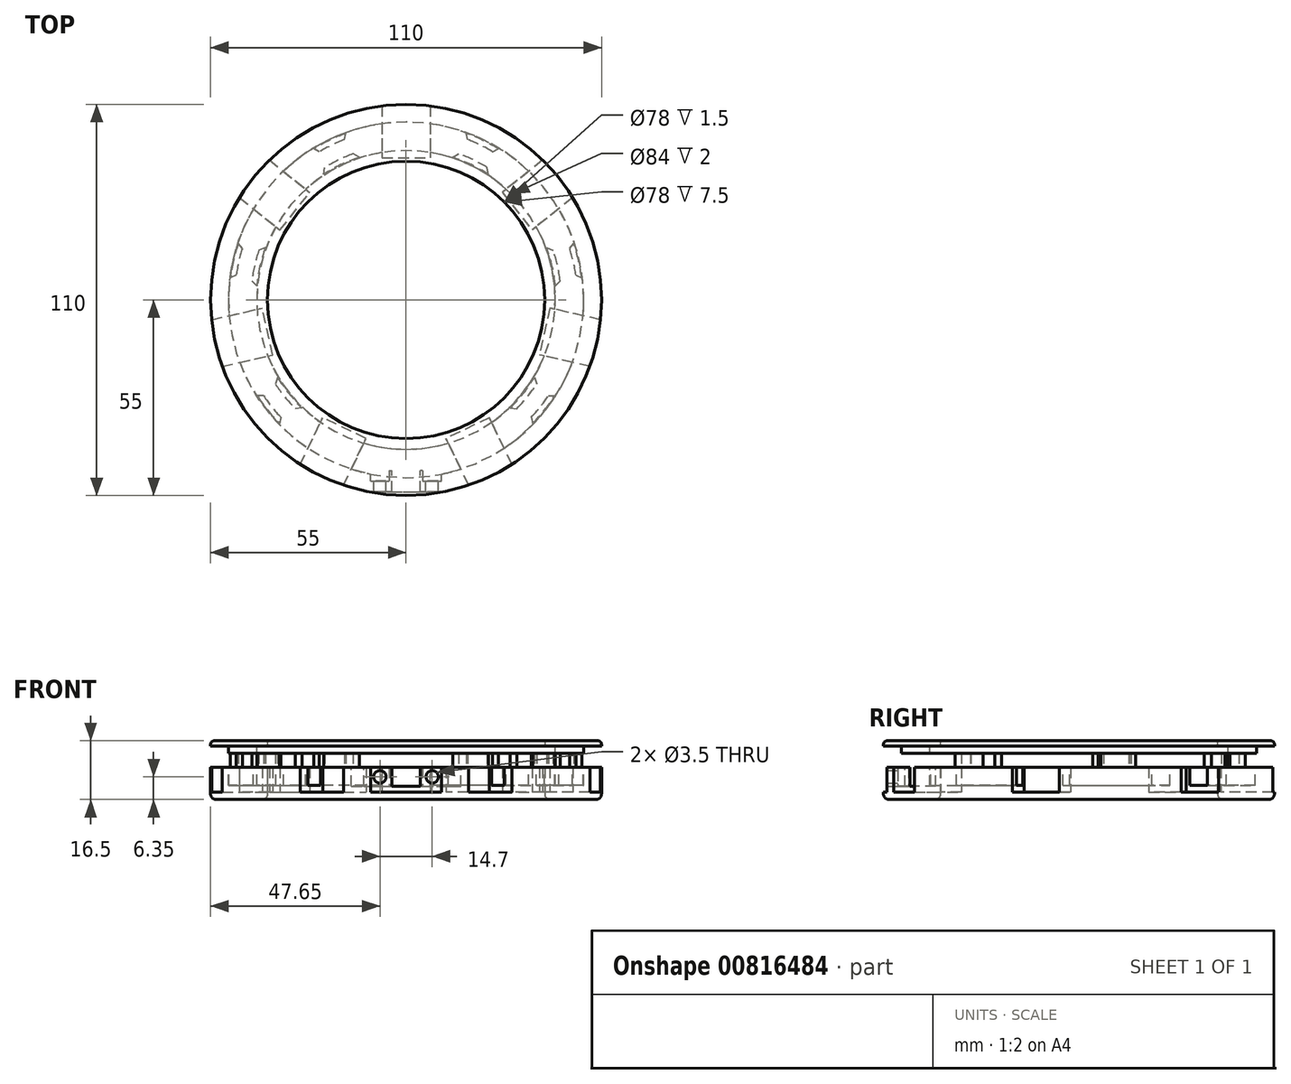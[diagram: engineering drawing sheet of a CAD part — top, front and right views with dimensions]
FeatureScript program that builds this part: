
annotation { "Feature Type Name" : "Feature", "Feature Type Description" : "" }
export const myFeature = defineFeature(function(context is Context, id is Id, definition is map)
    precondition{}
    {
        {
            var Q0;
            Q0=qCreatedBy(makeId("Top.planeOp"),FACE);
            var sketch = newSketch(context, id + "F0", { "sketchPlane" : qUnion([Q0])});
            skCircle(sketch, "E0", {"center": v(0, 0) * mm, "radius": 55 * mm});
            skCircle(sketch, "E1", {"center": v(0, 0) * mm, "radius": 39 * mm});
            skSolve(sketch);
        }
        {
            var Q0;
            Q0 = qSketchRegion(id + "F0", true);
            extrude(context, id + "F1", {"entities" : qUnion([Q0]), "depth" : 2 * mm, "offsetDistance" : 25 * mm});
        }
        {
            var Q0;
            Q0=makeQuery(id+"F1.opExtrude","CAP_FACE",FACE,{"disambiguationData":[OSD([sQuery(id+"F0.wireOp",EDGE,"E0"),sQuery(id+"F0.wireOp",EDGE,"E1")])],"isStart":false});
            var sketch = newSketch(context, id + "F2", { "sketchPlane" : qUnion([Q0])});
            skLineSegment(sketch, "E2.bottom", {"start": v(-6.75, 55) * mm, "end": v(6.75, 55) * mm});
            skLineSegment(sketch, "E2.top", {"start": v(-6.75, 40) * mm, "end": v(6.75, 40) * mm});
            skLineSegment(sketch, "E2.left", {"start": v(-6.75, 55) * mm, "end": v(-6.75, 40) * mm});
            skLineSegment(sketch, "E2.right", {"start": v(6.75, 55) * mm, "end": v(6.75, 40) * mm});
            skPoint(sketch, "E3", {"position": v(0, 55) * mm});
            skLineSegment(sketch, "E4.1.0", {"start": v(-47.2, 29.01) * mm, "end": v(-35.48, 19.66) * mm});
            skLineSegment(sketch, "E4.1.1", {"start": v(-47.2, 29.01) * mm, "end": v(-38.8, 39.57) * mm});
            skLineSegment(sketch, "E4.1.2", {"start": v(-38.8, 39.57) * mm, "end": v(-27.06, 30.22) * mm});
            skLineSegment(sketch, "E4.1.3", {"start": v(-35.48, 19.66) * mm, "end": v(-27.06, 30.22) * mm});
            skLineSegment(sketch, "E4.2.0", {"start": v(-52.12, -18.82) * mm, "end": v(-37.5, -15.48) * mm});
            skLineSegment(sketch, "E4.2.1", {"start": v(-52.12, -18.82) * mm, "end": v(-55.12, -5.66) * mm});
            skLineSegment(sketch, "E4.2.2", {"start": v(-55.12, -5.66) * mm, "end": v(-40.5, -2.32) * mm});
            skLineSegment(sketch, "E4.2.3", {"start": v(-37.5, -15.48) * mm, "end": v(-40.5, -2.32) * mm});
            skLineSegment(sketch, "E4.3.0", {"start": v(-17.78, -52.48) * mm, "end": v(-11.27, -38.97) * mm});
            skLineSegment(sketch, "E4.3.1", {"start": v(-17.78, -52.48) * mm, "end": v(-29.95, -46.62) * mm});
            skLineSegment(sketch, "E4.3.2", {"start": v(-29.95, -46.62) * mm, "end": v(-23.44, -33.11) * mm});
            skLineSegment(sketch, "E4.3.3", {"start": v(-11.27, -38.97) * mm, "end": v(-23.44, -33.11) * mm});
            skLineSegment(sketch, "E4.4.0", {"start": v(29.95, -46.62) * mm, "end": v(23.44, -33.11) * mm});
            skLineSegment(sketch, "E4.4.1", {"start": v(29.95, -46.62) * mm, "end": v(17.78, -52.48) * mm});
            skLineSegment(sketch, "E4.4.2", {"start": v(17.78, -52.48) * mm, "end": v(11.27, -38.97) * mm});
            skLineSegment(sketch, "E4.4.3", {"start": v(23.44, -33.11) * mm, "end": v(11.27, -38.97) * mm});
            skLineSegment(sketch, "E4.5.0", {"start": v(55.12, -5.66) * mm, "end": v(40.5, -2.32) * mm});
            skLineSegment(sketch, "E4.5.1", {"start": v(55.12, -5.66) * mm, "end": v(52.12, -18.82) * mm});
            skLineSegment(sketch, "E4.5.2", {"start": v(52.12, -18.82) * mm, "end": v(37.5, -15.48) * mm});
            skLineSegment(sketch, "E4.5.3", {"start": v(40.5, -2.32) * mm, "end": v(37.5, -15.48) * mm});
            skLineSegment(sketch, "E4.6.0", {"start": v(38.8, 39.57) * mm, "end": v(27.06, 30.22) * mm});
            skLineSegment(sketch, "E4.6.1", {"start": v(38.8, 39.57) * mm, "end": v(47.2, 29.01) * mm});
            skLineSegment(sketch, "E4.6.2", {"start": v(47.2, 29.01) * mm, "end": v(35.48, 19.66) * mm});
            skLineSegment(sketch, "E4.6.3", {"start": v(27.06, 30.22) * mm, "end": v(35.48, 19.66) * mm});
            skPoint(sketch, "E4.center", {"position": v(0, 0) * mm});
            skSolve(sketch);
        }
        {
            var Q0;
            {var subQ10=sQuery(id+"F2.wireOp",EDGE,"E2.top");Q0=makeQuery(id+"F2.imprint","IMPRINT",FACE,{"disambiguationData":[TD([[makeQuery(id+"F2.imprint","IMPRINT",EDGE,{"derivedFrom":subQ10}),-1.0]])]});}
            extrude(context, id + "F3", {"entities" : qUnion([Q0]), "operationType" : NewBodyOperationType.ADD, "depth" : 7 * mm, "offsetDistance" : 25 * mm});
        }
        {
            var Q0;
            Q0=makeQuery(id+"F3.opExtrude","CAP_FACE",FACE,{"disambiguationData":[OSD([sQuery(id+"F0.wireOp",EDGE,"E0"),sQuery(id+"F0.wireOp",EDGE,"E1"),sQuery(id+"F2.wireOp",EDGE,"E2.top"),sQuery(id+"F2.wireOp",EDGE,"E2.left"),sQuery(id+"F2.wireOp",EDGE,"E2.right"),sQuery(id+"F2.wireOp",EDGE,"E4.1.0"),sQuery(id+"F2.wireOp",EDGE,"E4.1.2"),sQuery(id+"F2.wireOp",EDGE,"E4.1.3"),sQuery(id+"F2.wireOp",EDGE,"E4.2.0"),sQuery(id+"F2.wireOp",EDGE,"E4.2.2"),sQuery(id+"F2.wireOp",EDGE,"E4.2.3"),sQuery(id+"F2.wireOp",EDGE,"E4.3.0"),sQuery(id+"F2.wireOp",EDGE,"E4.3.2"),sQuery(id+"F2.wireOp",EDGE,"E4.3.3"),sQuery(id+"F2.wireOp",EDGE,"E4.4.0"),sQuery(id+"F2.wireOp",EDGE,"E4.4.2"),sQuery(id+"F2.wireOp",EDGE,"E4.4.3"),sQuery(id+"F2.wireOp",EDGE,"E4.5.0"),sQuery(id+"F2.wireOp",EDGE,"E4.5.2"),sQuery(id+"F2.wireOp",EDGE,"E4.5.3"),sQuery(id+"F2.wireOp",EDGE,"E4.6.0"),sQuery(id+"F2.wireOp",EDGE,"E4.6.2"),sQuery(id+"F2.wireOp",EDGE,"E4.6.3")])],"isStart":false});
            var sketch = newSketch(context, id + "F4", { "sketchPlane" : qUnion([Q0])});
            skCircle(sketch, "E5", {"center": v(0, 0) * mm, "radius": 50 * mm});
            skCircle(sketch, "E6", {"center": v(0, 0) * mm, "radius": 42 * mm});
            skSolve(sketch);
        }
        {
            var Q0;
            Q0 = qSketchRegion(id + "F4", true);
            var Q1;
            {var subQ0=sQuery(id+"F0.wireOp",EDGE,"E0");Q1=makeQuery(id+"F3.boolean.opBoolean","SPLIT",FACE,{"disambiguationData":[TD([makeQuery(id+"F3.opExtrude","SWEPT_FACE",FACE,{"disambiguationData":[OSD([sQuery(id+"F2.wireOp",EDGE,"E2.top")])]})])],"derivedFrom":makeQuery(id+"F1.opExtrude","CAP_FACE",FACE,{"disambiguationData":[OSD([subQ0,sQuery(id+"F0.wireOp",EDGE,"E1")])],"isStart":false})});}
            extrude(context, id + "F5", {"entities" : qUnion([Q0]), "operationType" : NewBodyOperationType.REMOVE, "endBound" : BoundingType.UP_TO_SURFACE, "oppositeDirection" : true, "depth" : 25 * mm, "endBoundEntityFace" : qUnion([Q1]), "hasOffset" : true, "offsetDistance" : 2 * mm});
        }
        {
            var Q0;
            {var subQ0=sQuery(id+"F2.wireOp",EDGE,"E4.5.0");var subQ1=sQuery(id+"F0.wireOp",EDGE,"E0");var subQ2=makeQuery(id+"F1.opExtrude","CAP_EDGE",EDGE,{"disambiguationData":[OSD([subQ1])],"isStart":false});var subQ3=sQuery(id+"F2.wireOp",EDGE,"E4.6.2");var subQ4=sQuery(id+"F2.wireOp",EDGE,"E4.4.0");var subQ5=sQuery(id+"F2.wireOp",EDGE,"E4.5.2");var subQ6=sQuery(id+"F2.wireOp",EDGE,"E4.3.0");var subQ7=sQuery(id+"F2.wireOp",EDGE,"E4.4.2");var subQ8=sQuery(id+"F2.wireOp",EDGE,"E4.2.0");var subQ9=sQuery(id+"F2.wireOp",EDGE,"E4.3.2");var subQ10=sQuery(id+"F2.wireOp",EDGE,"E2.right");var subQ11=sQuery(id+"F2.wireOp",EDGE,"E4.6.0");var subQ12=sQuery(id+"F2.wireOp",EDGE,"E4.1.0");var subQ13=sQuery(id+"F2.wireOp",EDGE,"E4.2.2");var subQ14=sQuery(id+"F2.wireOp",EDGE,"E2.left");var subQ15=sQuery(id+"F2.wireOp",EDGE,"E4.1.2");Q0=makeQuery(id+"F5.boolean.opBoolean","SPLIT",FACE,{"disambiguationData":[TD([makeQuery(id+"F1.opExtrude","SWEPT_FACE",FACE,{"disambiguationData":[OSD([subQ1])]}),makeQuery(id+"F3.opExtrude","SWEPT_FACE",FACE,{"disambiguationData":[OSD([subQ6])]}),makeQuery(id+"F3.opExtrude","SWEPT_FACE",FACE,{"disambiguationData":[OSD([subQ7])]}),makeQuery(id+"F3.opExtrude","SWEPT_FACE",FACE,{"disambiguationData":[OSD([subQ1]),TDD([makeQuery(id+"F2.imprint","IMPRINT",EDGE,{"disambiguationData":[TD([[makeQuery(id+"F2.imprint","INTERSECT",VERTEX,{"derivedFrom":[subQ2,subQ14]}),-1.0]])],"derivedFrom":subQ2})])]}),makeQuery(id+"F3.opExtrude","SWEPT_FACE",FACE,{"disambiguationData":[OSD([subQ1]),TDD([makeQuery(id+"F2.imprint","IMPRINT",EDGE,{"disambiguationData":[TD([[makeQuery(id+"F2.imprint","INTERSECT",VERTEX,{"derivedFrom":[subQ2,subQ10]}),1.0]])],"derivedFrom":subQ2})])]}),makeQuery(id+"F3.opExtrude","SWEPT_FACE",FACE,{"disambiguationData":[OSD([subQ1]),TDD([makeQuery(id+"F2.imprint","IMPRINT",EDGE,{"disambiguationData":[TD([[makeQuery(id+"F2.imprint","INTERSECT",VERTEX,{"derivedFrom":[subQ2,subQ12]}),-1.0]])],"derivedFrom":subQ2})])]}),makeQuery(id+"F3.opExtrude","SWEPT_FACE",FACE,{"disambiguationData":[OSD([subQ1]),TDD([makeQuery(id+"F2.imprint","IMPRINT",EDGE,{"disambiguationData":[TD([[makeQuery(id+"F2.imprint","INTERSECT",VERTEX,{"derivedFrom":[subQ2,subQ8]}),-1.0]])],"derivedFrom":subQ2})])]}),makeQuery(id+"F3.opExtrude","SWEPT_FACE",FACE,{"disambiguationData":[OSD([subQ1]),TDD([makeQuery(id+"F2.imprint","IMPRINT",EDGE,{"disambiguationData":[TD([[makeQuery(id+"F2.imprint","INTERSECT",VERTEX,{"derivedFrom":[subQ2,subQ6]}),-1.0]])],"derivedFrom":subQ2})])]}),makeQuery(id+"F3.opExtrude","SWEPT_FACE",FACE,{"disambiguationData":[OSD([subQ1]),TDD([makeQuery(id+"F2.imprint","IMPRINT",EDGE,{"disambiguationData":[TD([[makeQuery(id+"F2.imprint","INTERSECT",VERTEX,{"derivedFrom":[subQ2,subQ4]}),-1.0]])],"derivedFrom":subQ2})])]}),makeQuery(id+"F3.opExtrude","SWEPT_FACE",FACE,{"disambiguationData":[OSD([subQ1]),TDD([makeQuery(id+"F2.imprint","IMPRINT",EDGE,{"disambiguationData":[TD([[makeQuery(id+"F2.imprint","INTERSECT",VERTEX,{"derivedFrom":[subQ2,subQ0]}),-1.0]])],"derivedFrom":subQ2})])]}),makeQuery(id+"F5.opExtrude","SWEPT_FACE",FACE,{"disambiguationData":[OSD([sQuery(id+"F4.wireOp",EDGE,"E5")])]})])],"derivedFrom":makeQuery(id+"F3.opExtrude","CAP_FACE",FACE,{"disambiguationData":[OSD([subQ1,sQuery(id+"F0.wireOp",EDGE,"E1"),sQuery(id+"F2.wireOp",EDGE,"E2.top"),subQ14,subQ10,subQ12,subQ15,sQuery(id+"F2.wireOp",EDGE,"E4.1.3"),subQ8,subQ13,sQuery(id+"F2.wireOp",EDGE,"E4.2.3"),subQ6,subQ9,sQuery(id+"F2.wireOp",EDGE,"E4.3.3"),subQ4,subQ7,sQuery(id+"F2.wireOp",EDGE,"E4.4.3"),subQ0,subQ5,sQuery(id+"F2.wireOp",EDGE,"E4.5.3"),subQ11,subQ3,sQuery(id+"F2.wireOp",EDGE,"E4.6.3")])],"isStart":false})});}
            var sketch = newSketch(context, id + "F6", { "sketchPlane" : qUnion([Q0])});
            skPoint(sketch, "E7.firstSnap0", {"position": v(0, -55) * mm});
            skLineSegment(sketch, "E7.bottom", {"start": v(10, -55) * mm, "end": v(-10, -55) * mm});
            skLineSegment(sketch, "E7.top", {"start": v(10, -54) * mm, "end": v(-10, -54) * mm});
            skLineSegment(sketch, "E7.left", {"start": v(10, -55) * mm, "end": v(10, -54) * mm});
            skLineSegment(sketch, "E7.right", {"start": v(-10, -55) * mm, "end": v(-10, -54) * mm});
            skLineSegment(sketch, "E8.bottom", {"start": v(-10, -51) * mm, "end": v(10, -51) * mm});
            skLineSegment(sketch, "E8.top", {"start": v(-10, -48.99) * mm, "end": v(10, -48.99) * mm});
            skLineSegment(sketch, "E8.left", {"start": v(-10, -51) * mm, "end": v(-10, -48.99) * mm});
            skLineSegment(sketch, "E8.right", {"start": v(10, -51) * mm, "end": v(10, -48.99) * mm});
            skSolve(sketch);
        }
        {
            var Q0;
            {var subQ7=sQuery(id+"F6.wireOp",EDGE,"E7.top");Q0=makeQuery(id+"F6.imprint","IMPRINT",FACE,{"disambiguationData":[TD([[makeQuery(id+"F6.imprint","IMPRINT",EDGE,{"derivedFrom":subQ7}),1.0]])]});}
            var Q1;
            {var subQ0=sQuery(id+"F0.wireOp",EDGE,"E0");var subQ2=sQuery(id+"F2.wireOp",EDGE,"E4.3.0");Q1=makeQuery(id+"F3.boolean.opBoolean","SPLIT",FACE,{"disambiguationData":[TD([makeQuery(id+"F3.opExtrude","SWEPT_FACE",FACE,{"disambiguationData":[OSD([subQ2])]})])],"derivedFrom":makeQuery(id+"F1.opExtrude","CAP_FACE",FACE,{"disambiguationData":[OSD([subQ0,sQuery(id+"F0.wireOp",EDGE,"E1")])],"isStart":false})});}
            extrude(context, id + "F7", {"entities" : qUnion([Q0]), "operationType" : NewBodyOperationType.REMOVE, "endBound" : BoundingType.UP_TO_SURFACE, "oppositeDirection" : true, "depth" : 25 * mm, "endBoundEntityFace" : qUnion([Q1]), "offsetDistance" : 25 * mm});
        }
        {
            var Q0;
            Q0=makeQuery(id+"F6.imprint","IMPRINT",FACE,{"disambiguationData":[TD([[makeQuery(id+"F6.imprint","IMPRINT",EDGE,{"derivedFrom":sQuery(id+"F6.wireOp",EDGE,"E8.bottom")}),1.0]])]});
            extrude(context, id + "F8", {"entities" : qUnion([Q0]), "operationType" : NewBodyOperationType.REMOVE, "oppositeDirection" : true, "depth" : 5.3 * mm, "offsetDistance" : 25 * mm});
        }
        {
            var Q0;
            {var subQ0=sQuery(id+"F2.wireOp",EDGE,"E4.5.0");var subQ1=sQuery(id+"F0.wireOp",EDGE,"E0");var subQ2=makeQuery(id+"F1.opExtrude","CAP_EDGE",EDGE,{"disambiguationData":[OSD([subQ1])],"isStart":false});var subQ3=sQuery(id+"F2.wireOp",EDGE,"E4.6.2");var subQ4=sQuery(id+"F2.wireOp",EDGE,"E4.4.0");var subQ5=sQuery(id+"F2.wireOp",EDGE,"E4.5.2");var subQ6=sQuery(id+"F2.wireOp",EDGE,"E4.3.0");var subQ7=sQuery(id+"F2.wireOp",EDGE,"E4.4.2");var subQ8=sQuery(id+"F2.wireOp",EDGE,"E4.2.0");var subQ9=sQuery(id+"F2.wireOp",EDGE,"E4.3.2");var subQ10=sQuery(id+"F2.wireOp",EDGE,"E2.right");var subQ11=sQuery(id+"F2.wireOp",EDGE,"E4.6.0");var subQ12=sQuery(id+"F2.wireOp",EDGE,"E4.1.0");var subQ13=sQuery(id+"F2.wireOp",EDGE,"E4.2.2");var subQ14=sQuery(id+"F2.wireOp",EDGE,"E2.left");var subQ15=sQuery(id+"F2.wireOp",EDGE,"E4.1.2");Q0=makeQuery(id+"F5.boolean.opBoolean","SPLIT",FACE,{"disambiguationData":[TD([makeQuery(id+"F1.opExtrude","SWEPT_FACE",FACE,{"disambiguationData":[OSD([subQ1])]}),makeQuery(id+"F3.opExtrude","SWEPT_FACE",FACE,{"disambiguationData":[OSD([subQ6])]}),makeQuery(id+"F3.opExtrude","SWEPT_FACE",FACE,{"disambiguationData":[OSD([subQ7])]}),makeQuery(id+"F3.opExtrude","SWEPT_FACE",FACE,{"disambiguationData":[OSD([subQ1]),TDD([makeQuery(id+"F2.imprint","IMPRINT",EDGE,{"disambiguationData":[TD([[makeQuery(id+"F2.imprint","INTERSECT",VERTEX,{"derivedFrom":[subQ2,subQ14]}),-1.0]])],"derivedFrom":subQ2})])]}),makeQuery(id+"F3.opExtrude","SWEPT_FACE",FACE,{"disambiguationData":[OSD([subQ1]),TDD([makeQuery(id+"F2.imprint","IMPRINT",EDGE,{"disambiguationData":[TD([[makeQuery(id+"F2.imprint","INTERSECT",VERTEX,{"derivedFrom":[subQ2,subQ10]}),1.0]])],"derivedFrom":subQ2})])]}),makeQuery(id+"F3.opExtrude","SWEPT_FACE",FACE,{"disambiguationData":[OSD([subQ1]),TDD([makeQuery(id+"F2.imprint","IMPRINT",EDGE,{"disambiguationData":[TD([[makeQuery(id+"F2.imprint","INTERSECT",VERTEX,{"derivedFrom":[subQ2,subQ12]}),-1.0]])],"derivedFrom":subQ2})])]}),makeQuery(id+"F3.opExtrude","SWEPT_FACE",FACE,{"disambiguationData":[OSD([subQ1]),TDD([makeQuery(id+"F2.imprint","IMPRINT",EDGE,{"disambiguationData":[TD([[makeQuery(id+"F2.imprint","INTERSECT",VERTEX,{"derivedFrom":[subQ2,subQ8]}),-1.0]])],"derivedFrom":subQ2})])]}),makeQuery(id+"F3.opExtrude","SWEPT_FACE",FACE,{"disambiguationData":[OSD([subQ1]),TDD([makeQuery(id+"F2.imprint","IMPRINT",EDGE,{"disambiguationData":[TD([[makeQuery(id+"F2.imprint","INTERSECT",VERTEX,{"derivedFrom":[subQ2,subQ6]}),-1.0]])],"derivedFrom":subQ2})])]}),makeQuery(id+"F3.opExtrude","SWEPT_FACE",FACE,{"disambiguationData":[OSD([subQ1]),TDD([makeQuery(id+"F2.imprint","IMPRINT",EDGE,{"disambiguationData":[TD([[makeQuery(id+"F2.imprint","INTERSECT",VERTEX,{"derivedFrom":[subQ2,subQ4]}),-1.0]])],"derivedFrom":subQ2})])]}),makeQuery(id+"F3.opExtrude","SWEPT_FACE",FACE,{"disambiguationData":[OSD([subQ1]),TDD([makeQuery(id+"F2.imprint","IMPRINT",EDGE,{"disambiguationData":[TD([[makeQuery(id+"F2.imprint","INTERSECT",VERTEX,{"derivedFrom":[subQ2,subQ0]}),-1.0]])],"derivedFrom":subQ2})])]}),makeQuery(id+"F5.opExtrude","SWEPT_FACE",FACE,{"disambiguationData":[OSD([sQuery(id+"F4.wireOp",EDGE,"E5")])]})])],"derivedFrom":makeQuery(id+"F3.opExtrude","CAP_FACE",FACE,{"disambiguationData":[OSD([subQ1,sQuery(id+"F0.wireOp",EDGE,"E1"),sQuery(id+"F2.wireOp",EDGE,"E2.top"),subQ14,subQ10,subQ12,subQ15,sQuery(id+"F2.wireOp",EDGE,"E4.1.3"),subQ8,subQ13,sQuery(id+"F2.wireOp",EDGE,"E4.2.3"),subQ6,subQ9,sQuery(id+"F2.wireOp",EDGE,"E4.3.3"),subQ4,subQ7,sQuery(id+"F2.wireOp",EDGE,"E4.4.3"),subQ0,subQ5,sQuery(id+"F2.wireOp",EDGE,"E4.5.3"),subQ11,subQ3,sQuery(id+"F2.wireOp",EDGE,"E4.6.3")])],"isStart":false})});}
            var sketch = newSketch(context, id + "F9", { "sketchPlane" : qUnion([Q0])});
            skLineSegment(sketch, "E9", {"start": v(-4, -51) * mm, "end": v(-4, -54) * mm});
            skLineSegment(sketch, "E10.MirrorCS", {"start": v(4, -51) * mm, "end": v(4, -54) * mm});
            skSolve(sketch);
        }
        {
            var Q0;
            {var subQ0=sQuery(id+"F9.wireOp",EDGE,"E9");Q0=makeQuery(id+"F9.imprint","IMPRINT",FACE,{"disambiguationData":[TD([[makeQuery(id+"F9.imprint","IMPRINT",EDGE,{"derivedFrom":subQ0}),1.0]])]});}
            var Q1;
            Q1=makeQuery(id+"F8.boolean.opBoolean","COPY",FACE,{"derivedFrom":makeQuery(id+"F8.opExtrude","CAP_FACE",FACE,{"disambiguationData":[OSD([sQuery(id+"F4.wireOp",EDGE,"E5"),sQuery(id+"F6.wireOp",EDGE,"E8.bottom"),sQuery(id+"F6.wireOp",EDGE,"E8.left"),sQuery(id+"F6.wireOp",EDGE,"E8.right")])],"isStart":false})});
            extrude(context, id + "F10", {"entities" : qUnion([Q0]), "operationType" : NewBodyOperationType.REMOVE, "endBound" : BoundingType.UP_TO_SURFACE, "oppositeDirection" : true, "depth" : 25 * mm, "endBoundEntityFace" : qUnion([Q1]), "offsetDistance" : 25 * mm});
        }
        {
            var Q0;
            {var subQ0=sQuery(id+"F4.wireOp",EDGE,"E5");var subQ1=sQuery(id+"F4.wireOp",EDGE,"E6");Q0=makeQuery(id+"F5.boolean.opBoolean","COPY",FACE,{"disambiguationData":[TD([makeQuery(id+"F3.opExtrude","SWEPT_FACE",FACE,{"disambiguationData":[OSD([sQuery(id+"F2.wireOp",EDGE,"E4.3.0")])]})])],"derivedFrom":makeQuery(id+"F5.opExtrude","CAP_FACE",FACE,{"disambiguationData":[OSD([subQ0,subQ1])],"isStart":false})});}
            var Q1;
            {var subQ0=sQuery(id+"F6.wireOp",EDGE,"E8.bottom");Q1=makeQuery(id+"F10.boolean.opBoolean","MERGE",FACE,{"derivedFrom":[makeQuery(id+"F8.boolean.opBoolean","COPY",FACE,{"derivedFrom":makeQuery(id+"F8.opExtrude","CAP_FACE",FACE,{"disambiguationData":[OSD([sQuery(id+"F4.wireOp",EDGE,"E5"),subQ0,sQuery(id+"F6.wireOp",EDGE,"E8.left"),sQuery(id+"F6.wireOp",EDGE,"E8.right")])],"isStart":false})})],"fromTools":[makeQuery(id+"F10.opExtrude","CAP_FACE",FACE,{"disambiguationData":[OSD([sQuery(id+"F6.wireOp",EDGE,"E7.top"),subQ0,sQuery(id+"F9.wireOp",EDGE,"E9"),sQuery(id+"F9.wireOp",EDGE,"E10.MirrorCS")])],"isStart":false})]});}
            extrude(context, id + "F11", {"entities" : qUnion([Q0]), "operationType" : NewBodyOperationType.REMOVE, "endBound" : BoundingType.UP_TO_SURFACE, "oppositeDirection" : true, "depth" : 25 * mm, "endBoundEntityFace" : qUnion([Q1]), "offsetDistance" : 25 * mm});
        }
        {
            var Q0;
            {var subQ0=sQuery(id+"F4.wireOp",EDGE,"E5");var subQ1=sQuery(id+"F6.wireOp",EDGE,"E8.bottom");Q0=makeQuery(id+"F11.boolean.opBoolean","MERGE",FACE,{"derivedFrom":[makeQuery(id+"F10.boolean.opBoolean","MERGE",FACE,{"derivedFrom":[makeQuery(id+"F8.boolean.opBoolean","COPY",FACE,{"derivedFrom":makeQuery(id+"F8.opExtrude","CAP_FACE",FACE,{"disambiguationData":[OSD([subQ0,subQ1,sQuery(id+"F6.wireOp",EDGE,"E8.left"),sQuery(id+"F6.wireOp",EDGE,"E8.right")])],"isStart":false})})],"fromTools":[makeQuery(id+"F10.opExtrude","CAP_FACE",FACE,{"disambiguationData":[OSD([sQuery(id+"F6.wireOp",EDGE,"E7.top"),subQ1,sQuery(id+"F9.wireOp",EDGE,"E9"),sQuery(id+"F9.wireOp",EDGE,"E10.MirrorCS")])],"isStart":false})]})],"fromTools":[makeQuery(id+"F11.opExtrude","CAP_FACE",FACE,{"disambiguationData":[OSD([subQ0,sQuery(id+"F4.wireOp",EDGE,"E6")])],"isStart":false})]});}
            var sketch = newSketch(context, id + "F12", { "sketchPlane" : qUnion([Q0])});
            skLineSegment(sketch, "E11.top", {"start": v(-4.7, -51) * mm, "end": v(-4, -51) * mm});
            skLineSegment(sketch, "E11.left", {"start": v(-4.7, -48) * mm, "end": v(-4.7, -51) * mm});
            skLineSegment(sketch, "E11.right", {"start": v(-4, -48) * mm, "end": v(-4, -51) * mm});
            skLineSegment(sketch, "E12", {"start": v(-4.7, -48) * mm, "end": v(-4, -48) * mm});
            skLineSegment(sketch, "E13.MirrorCS", {"start": v(4.7, -51) * mm, "end": v(4, -51) * mm});
            skLineSegment(sketch, "E14.MirrorCS", {"start": v(4.7, -48) * mm, "end": v(4, -48) * mm});
            skLineSegment(sketch, "E15.MirrorCS", {"start": v(4, -48) * mm, "end": v(4, -51) * mm});
            skLineSegment(sketch, "E16.MirrorCS", {"start": v(4.7, -48) * mm, "end": v(4.7, -51) * mm});
            skSolve(sketch);
        }
        {
            var Q0;
            Q0 = qSketchRegion(id + "F12", true);
            var Q1;
            {var subQ0=sQuery(id+"F2.wireOp",EDGE,"E4.5.0");var subQ1=sQuery(id+"F0.wireOp",EDGE,"E0");var subQ2=makeQuery(id+"F1.opExtrude","CAP_EDGE",EDGE,{"disambiguationData":[OSD([subQ1])],"isStart":false});var subQ3=sQuery(id+"F2.wireOp",EDGE,"E4.6.2");var subQ4=makeQuery(id+"F3.opExtrude","SWEPT_FACE",FACE,{"disambiguationData":[OSD([subQ1]),TDD([makeQuery(id+"F2.imprint","IMPRINT",EDGE,{"disambiguationData":[TD([[makeQuery(id+"F2.imprint","INTERSECT",VERTEX,{"derivedFrom":[subQ2,subQ0]}),-1.0]])],"derivedFrom":subQ2})])]});var subQ5=sQuery(id+"F2.wireOp",EDGE,"E4.4.0");var subQ6=sQuery(id+"F2.wireOp",EDGE,"E4.5.2");var subQ7=makeQuery(id+"F3.opExtrude","SWEPT_FACE",FACE,{"disambiguationData":[OSD([subQ1]),TDD([makeQuery(id+"F2.imprint","IMPRINT",EDGE,{"disambiguationData":[TD([[makeQuery(id+"F2.imprint","INTERSECT",VERTEX,{"derivedFrom":[subQ2,subQ5]}),-1.0]])],"derivedFrom":subQ2})])]});var subQ8=sQuery(id+"F2.wireOp",EDGE,"E4.3.0");var subQ9=sQuery(id+"F2.wireOp",EDGE,"E4.4.2");var subQ10=makeQuery(id+"F3.opExtrude","SWEPT_FACE",FACE,{"disambiguationData":[OSD([subQ1]),TDD([makeQuery(id+"F2.imprint","IMPRINT",EDGE,{"disambiguationData":[TD([[makeQuery(id+"F2.imprint","INTERSECT",VERTEX,{"derivedFrom":[subQ2,subQ8]}),-1.0]])],"derivedFrom":subQ2})])]});var subQ11=sQuery(id+"F2.wireOp",EDGE,"E4.2.0");var subQ12=sQuery(id+"F2.wireOp",EDGE,"E4.3.2");var subQ13=makeQuery(id+"F3.opExtrude","SWEPT_FACE",FACE,{"disambiguationData":[OSD([subQ1]),TDD([makeQuery(id+"F2.imprint","IMPRINT",EDGE,{"disambiguationData":[TD([[makeQuery(id+"F2.imprint","INTERSECT",VERTEX,{"derivedFrom":[subQ2,subQ11]}),-1.0]])],"derivedFrom":subQ2})])]});var subQ14=sQuery(id+"F2.wireOp",EDGE,"E4.1.0");var subQ15=sQuery(id+"F2.wireOp",EDGE,"E4.2.2");var subQ16=makeQuery(id+"F3.opExtrude","SWEPT_FACE",FACE,{"disambiguationData":[OSD([subQ1]),TDD([makeQuery(id+"F2.imprint","IMPRINT",EDGE,{"disambiguationData":[TD([[makeQuery(id+"F2.imprint","INTERSECT",VERTEX,{"derivedFrom":[subQ2,subQ14]}),-1.0]])],"derivedFrom":subQ2})])]});var subQ17=makeQuery(id+"F1.opExtrude","SWEPT_FACE",FACE,{"disambiguationData":[OSD([subQ1])]});var subQ18=makeQuery(id+"F3.opExtrude","SWEPT_FACE",FACE,{"disambiguationData":[OSD([subQ8])]});var subQ19=sQuery(id+"F2.wireOp",EDGE,"E4.6.0");var subQ20=sQuery(id+"F2.wireOp",EDGE,"E4.1.2");var subQ21=sQuery(id+"F2.wireOp",EDGE,"E2.right");var subQ22=sQuery(id+"F2.wireOp",EDGE,"E2.left");var subQ23=makeQuery(id+"F3.opExtrude","CAP_FACE",FACE,{"disambiguationData":[OSD([subQ1,sQuery(id+"F0.wireOp",EDGE,"E1"),sQuery(id+"F2.wireOp",EDGE,"E2.top"),subQ22,subQ21,subQ14,subQ20,sQuery(id+"F2.wireOp",EDGE,"E4.1.3"),subQ11,subQ15,sQuery(id+"F2.wireOp",EDGE,"E4.2.3"),subQ8,subQ12,sQuery(id+"F2.wireOp",EDGE,"E4.3.3"),subQ5,subQ9,sQuery(id+"F2.wireOp",EDGE,"E4.4.3"),subQ0,subQ6,sQuery(id+"F2.wireOp",EDGE,"E4.5.3"),subQ19,subQ3,sQuery(id+"F2.wireOp",EDGE,"E4.6.3")])],"isStart":false});var subQ24=sQuery(id+"F4.wireOp",EDGE,"E5");var subQ25=makeQuery(id+"F3.opExtrude","SWEPT_FACE",FACE,{"disambiguationData":[OSD([subQ9])]});var subQ26=makeQuery(id+"F5.opExtrude","SWEPT_FACE",FACE,{"disambiguationData":[OSD([subQ24])]});var subQ27=makeQuery(id+"F3.opExtrude","SWEPT_FACE",FACE,{"disambiguationData":[OSD([subQ1]),TDD([makeQuery(id+"F2.imprint","IMPRINT",EDGE,{"disambiguationData":[TD([[makeQuery(id+"F2.imprint","INTERSECT",VERTEX,{"derivedFrom":[subQ2,subQ21]}),1.0]])],"derivedFrom":subQ2})])]});var subQ28=makeQuery(id+"F3.opExtrude","SWEPT_FACE",FACE,{"disambiguationData":[OSD([subQ1]),TDD([makeQuery(id+"F2.imprint","IMPRINT",EDGE,{"disambiguationData":[TD([[makeQuery(id+"F2.imprint","INTERSECT",VERTEX,{"derivedFrom":[subQ2,subQ22]}),-1.0]])],"derivedFrom":subQ2})])]});Q1=makeQuery(id+"F10.boolean.opBoolean","SPLIT",FACE,{"disambiguationData":[TD([subQ18])],"derivedFrom":makeQuery(id+"F5.boolean.opBoolean","SPLIT",FACE,{"disambiguationData":[TD([subQ17,subQ18,subQ25,subQ28,subQ27,subQ16,subQ13,subQ10,subQ7,subQ4,subQ26])],"derivedFrom":subQ23})});}
            extrude(context, id + "F13", {"entities" : qUnion([Q0]), "operationType" : NewBodyOperationType.ADD, "endBound" : BoundingType.UP_TO_SURFACE, "depth" : 25 * mm, "endBoundEntityFace" : qUnion([Q1]), "offsetDistance" : 25 * mm});
        }
        {
            var Q0;
            {var subQ1=sQuery(id+"F6.wireOp",EDGE,"E8.left");var subQ2=sQuery(id+"F6.wireOp",EDGE,"E8.bottom");Q0=makeQuery(id+"F10.boolean.opBoolean","SPLIT",FACE,{"disambiguationData":[TD([makeQuery(id+"F8.boolean.opBoolean","COPY",FACE,{"derivedFrom":makeQuery(id+"F8.opExtrude","SWEPT_FACE",FACE,{"disambiguationData":[OSD([subQ1])]})})])],"derivedFrom":makeQuery(id+"F8.boolean.opBoolean","COPY",FACE,{"derivedFrom":makeQuery(id+"F8.opExtrude","SWEPT_FACE",FACE,{"disambiguationData":[OSD([subQ2])]})})});}
            var sketch = newSketch(context, id + "F14", { "sketchPlane" : qUnion([Q0])});
            skCircle(sketch, "E17", {"center": v(7.35, 6.35) * mm, "radius": 1.75 * mm});
            skPoint(sketch, "E17.centerSnap0", {"position": v(10, 6.35) * mm});
            skPoint(sketch, "E17.centerSnap1", {"position": v(7.35, 9) * mm});
            skCircle(sketch, "E18.MirrorC", {"center": v(-7.35, 6.35) * mm, "radius": 1.75 * mm});
            skSolve(sketch);
        }
        {
            var Q0;
            Q0 = qSketchRegion(id + "F14", true);
            var Q1;
            Q1=makeQuery(id+"F7.boolean.opBoolean","COPY",FACE,{"derivedFrom":makeQuery(id+"F7.opExtrude","SWEPT_FACE",FACE,{"disambiguationData":[OSD([sQuery(id+"F6.wireOp",EDGE,"E7.top")])]})});
            extrude(context, id + "F15", {"entities" : qUnion([Q0]), "operationType" : NewBodyOperationType.REMOVE, "endBound" : BoundingType.UP_TO_SURFACE, "oppositeDirection" : true, "depth" : 25 * mm, "endBoundEntityFace" : qUnion([Q1]), "offsetDistance" : 25 * mm});
        }
        {
            var Q0;
            Q0=makeQuery(id+"F1.opExtrude","CAP_EDGE",EDGE,{"disambiguationData":[OSD([sQuery(id+"F0.wireOp",EDGE,"E0")])],"isStart":true});
            var Q1;
            Q1=makeQuery(id+"F1.opExtrude","CAP_EDGE",EDGE,{"disambiguationData":[OSD([sQuery(id+"F0.wireOp",EDGE,"E1")])],"isStart":true});
            fillet(context, id + "F16", {"entities" : qUnion([Q0, Q1]), "radius" : 1.5 * mm, "tangentPropagation" : true, "allowEdgeOverflow" : false});
        }
        {
            var Q0;
            {var subQ1=sQuery(id+"F2.wireOp",EDGE,"E2.left");var subQ7=sQuery(id+"F0.wireOp",EDGE,"E0");var subQ8=makeQuery(id+"F1.opExtrude","CAP_EDGE",EDGE,{"disambiguationData":[OSD([subQ7])],"isStart":false});var subQ9=makeQuery(id+"F3.opExtrude","CAP_EDGE",EDGE,{"disambiguationData":[OSD([subQ7]),TDD([makeQuery(id+"F2.imprint","IMPRINT",EDGE,{"disambiguationData":[TD([[makeQuery(id+"F2.imprint","INTERSECT",VERTEX,{"derivedFrom":[subQ8,subQ1]}),-1.0]])],"derivedFrom":subQ8})])],"isStart":false});Q0=makeQuery(id+"F4.imprint","IMPRINT",FACE,{"disambiguationData":[TD([[makeQuery(id+"F4.imprint","IMPRINT",EDGE,{"derivedFrom":subQ9}),1.0]])]});}
            var sketch = newSketch(context, id + "F17", { "sketchPlane" : qUnion([Q0])});
            skPoint(sketch, "E19.0", {"position": v(0, 55) * mm});
            skArc(sketch, "E20", {"start": v(-17, 46.81) * mm, "mid": v(-21.6, 44.87) * mm, "end": v(-26, 42.47) * mm});
            skArc(sketch, "E21", {"start": v(-13.15, 40.1) * mm, "mid": v(-18.3, 38.02) * mm, "end": v(-23.15, 35.28) * mm});
            skArc(sketch, "E22", {"start": v(-17.39, 45.06) * mm, "mid": v(-20.96, 43.52) * mm, "end": v(-24.39, 41.7) * mm});
            skArc(sketch, "E23", {"start": v(-22.86, 37.24) * mm, "mid": v(-18.96, 39.37) * mm, "end": v(-14.86, 41.1) * mm});
            skLineSegment(sketch, "E24", {"start": v(-26, 42.47) * mm, "end": v(-24.39, 41.7) * mm});
            skLineSegment(sketch, "E25", {"start": v(-17, 46.81) * mm, "end": v(-17.39, 45.06) * mm});
            skLineSegment(sketch, "E26", {"start": v(-22.86, 37.24) * mm, "end": v(-23.15, 35.28) * mm});
            skLineSegment(sketch, "E27", {"start": v(-14.86, 41.1) * mm, "end": v(-13.15, 40.1) * mm});
            skPoint(sketch, "E28", {"position": v(-18.3, 38.02) * mm});
            skPoint(sketch, "E29", {"position": v(-18.96, 39.37) * mm});
            skPoint(sketch, "E30", {"position": v(-20.96, 43.52) * mm});
            skPoint(sketch, "E31", {"position": v(-21.6, 44.87) * mm});
            skLineSegment(sketch, "E32", {"start": v(-21.6, 44.87) * mm, "end": v(0, 0) * mm, "construction": true});
            skArc(sketch, "E33.1.0", {"start": v(-46.07, 14.5) * mm, "mid": v(-47.09, 10.75) * mm, "end": v(-47.8, 6.93) * mm});
            skArc(sketch, "E33.1.1", {"start": v(-43.37, 5.35) * mm, "mid": v(-42.6, 9.72) * mm, "end": v(-41.4, 14) * mm});
            skArc(sketch, "E33.1.2", {"start": v(-39.55, 14.72) * mm, "mid": v(-41.14, 9.4) * mm, "end": v(-42.02, 3.9) * mm});
            skLineSegment(sketch, "E33.1.3", {"start": v(-49.42, 6.15) * mm, "end": v(-47.8, 6.93) * mm});
            skArc(sketch, "E33.1.4", {"start": v(-47.2, 15.9) * mm, "mid": v(-48.55, 11.08) * mm, "end": v(-49.42, 6.15) * mm});
            skLineSegment(sketch, "E33.1.5", {"start": v(-47.2, 15.9) * mm, "end": v(-46.07, 14.5) * mm});
            skLineSegment(sketch, "E33.1.6", {"start": v(-43.37, 5.35) * mm, "end": v(-42.02, 3.9) * mm});
            skLineSegment(sketch, "E33.1.7", {"start": v(-41.4, 14) * mm, "end": v(-39.55, 14.72) * mm});
            skPoint(sketch, "E33.1.8", {"position": v(-42.6, 9.72) * mm});
            skPoint(sketch, "E33.1.9", {"position": v(-47.09, 10.75) * mm});
            skPoint(sketch, "E33.1.10", {"position": v(-48.55, 11.08) * mm});
            skPoint(sketch, "E33.1.11", {"position": v(-41.14, 9.4) * mm});
            skArc(sketch, "E33.2.0", {"start": v(-40.06, -26.98) * mm, "mid": v(-37.76, -30.11) * mm, "end": v(-35.22, -33.05) * mm});
            skArc(sketch, "E33.2.1", {"start": v(-31.22, -30.58) * mm, "mid": v(-34.17, -27.25) * mm, "end": v(-36.76, -23.63) * mm});
            skArc(sketch, "E33.2.2", {"start": v(-36.17, -21.74) * mm, "mid": v(-33, -26.31) * mm, "end": v(-29.25, -30.42) * mm});
            skLineSegment(sketch, "E33.2.3", {"start": v(-35.62, -34.8) * mm, "end": v(-35.22, -33.05) * mm});
            skArc(sketch, "E33.2.4", {"start": v(-41.86, -26.98) * mm, "mid": v(-38.94, -31.05) * mm, "end": v(-35.62, -34.8) * mm});
            skLineSegment(sketch, "E33.2.5", {"start": v(-41.86, -26.98) * mm, "end": v(-40.06, -26.98) * mm});
            skLineSegment(sketch, "E33.2.6", {"start": v(-31.22, -30.58) * mm, "end": v(-29.25, -30.42) * mm});
            skLineSegment(sketch, "E33.2.7", {"start": v(-36.76, -23.63) * mm, "end": v(-36.17, -21.74) * mm});
            skPoint(sketch, "E33.2.8", {"position": v(-34.17, -27.25) * mm});
            skPoint(sketch, "E33.2.9", {"position": v(-37.76, -30.11) * mm});
            skPoint(sketch, "E33.2.10", {"position": v(-38.94, -31.05) * mm});
            skPoint(sketch, "E33.2.11", {"position": v(-33, -26.31) * mm});
            skArc(sketch, "E33.4.0", {"start": v(35.22, -33.05) * mm, "mid": v(37.76, -30.11) * mm, "end": v(40.06, -26.98) * mm});
            skArc(sketch, "E33.4.1", {"start": v(36.76, -23.63) * mm, "mid": v(34.17, -27.25) * mm, "end": v(31.22, -30.58) * mm});
            skArc(sketch, "E33.4.2", {"start": v(29.25, -30.42) * mm, "mid": v(33, -26.31) * mm, "end": v(36.17, -21.74) * mm});
            skLineSegment(sketch, "E33.4.3", {"start": v(41.86, -26.98) * mm, "end": v(40.06, -26.98) * mm});
            skArc(sketch, "E33.4.4", {"start": v(35.62, -34.8) * mm, "mid": v(38.94, -31.05) * mm, "end": v(41.86, -26.98) * mm});
            skLineSegment(sketch, "E33.4.5", {"start": v(35.62, -34.8) * mm, "end": v(35.22, -33.05) * mm});
            skLineSegment(sketch, "E33.4.6", {"start": v(36.76, -23.63) * mm, "end": v(36.17, -21.74) * mm});
            skLineSegment(sketch, "E33.4.7", {"start": v(31.22, -30.58) * mm, "end": v(29.25, -30.42) * mm});
            skPoint(sketch, "E33.4.8", {"position": v(34.17, -27.25) * mm});
            skPoint(sketch, "E33.4.9", {"position": v(37.76, -30.11) * mm});
            skPoint(sketch, "E33.4.10", {"position": v(38.94, -31.05) * mm});
            skPoint(sketch, "E33.4.11", {"position": v(33, -26.31) * mm});
            skArc(sketch, "E33.5.0", {"start": v(47.8, 6.93) * mm, "mid": v(47.09, 10.75) * mm, "end": v(46.07, 14.5) * mm});
            skArc(sketch, "E33.5.1", {"start": v(41.4, 14) * mm, "mid": v(42.6, 9.72) * mm, "end": v(43.37, 5.35) * mm});
            skArc(sketch, "E33.5.2", {"start": v(42.02, 3.9) * mm, "mid": v(41.14, 9.4) * mm, "end": v(39.55, 14.72) * mm});
            skLineSegment(sketch, "E33.5.3", {"start": v(47.2, 15.9) * mm, "end": v(46.07, 14.5) * mm});
            skArc(sketch, "E33.5.4", {"start": v(49.42, 6.15) * mm, "mid": v(48.55, 11.08) * mm, "end": v(47.2, 15.9) * mm});
            skLineSegment(sketch, "E33.5.5", {"start": v(49.42, 6.15) * mm, "end": v(47.8, 6.93) * mm});
            skLineSegment(sketch, "E33.5.6", {"start": v(41.4, 14) * mm, "end": v(39.55, 14.72) * mm});
            skLineSegment(sketch, "E33.5.7", {"start": v(43.37, 5.35) * mm, "end": v(42.02, 3.9) * mm});
            skPoint(sketch, "E33.5.8", {"position": v(42.6, 9.72) * mm});
            skPoint(sketch, "E33.5.9", {"position": v(47.09, 10.75) * mm});
            skPoint(sketch, "E33.5.10", {"position": v(48.55, 11.08) * mm});
            skPoint(sketch, "E33.5.11", {"position": v(41.14, 9.4) * mm});
            skArc(sketch, "E33.6.0", {"start": v(24.39, 41.7) * mm, "mid": v(20.96, 43.52) * mm, "end": v(17.39, 45.06) * mm});
            skArc(sketch, "E33.6.1", {"start": v(14.86, 41.1) * mm, "mid": v(18.96, 39.37) * mm, "end": v(22.86, 37.24) * mm});
            skArc(sketch, "E33.6.2", {"start": v(23.15, 35.28) * mm, "mid": v(18.3, 38.02) * mm, "end": v(13.15, 40.1) * mm});
            skLineSegment(sketch, "E33.6.3", {"start": v(17, 46.81) * mm, "end": v(17.39, 45.06) * mm});
            skArc(sketch, "E33.6.4", {"start": v(26, 42.47) * mm, "mid": v(21.6, 44.87) * mm, "end": v(17, 46.81) * mm});
            skLineSegment(sketch, "E33.6.5", {"start": v(26, 42.47) * mm, "end": v(24.39, 41.7) * mm});
            skLineSegment(sketch, "E33.6.6", {"start": v(14.86, 41.1) * mm, "end": v(13.15, 40.1) * mm});
            skLineSegment(sketch, "E33.6.7", {"start": v(22.86, 37.24) * mm, "end": v(23.15, 35.28) * mm});
            skPoint(sketch, "E33.6.8", {"position": v(18.96, 39.37) * mm});
            skPoint(sketch, "E33.6.9", {"position": v(20.96, 43.52) * mm});
            skPoint(sketch, "E33.6.10", {"position": v(21.6, 44.87) * mm});
            skPoint(sketch, "E33.6.11", {"position": v(18.3, 38.02) * mm});
            skSolve(sketch);
        }
        {
            var Q0;
            Q0 = qSketchRegion(id + "F17", true);
            extrude(context, id + "F18", {"entities" : qUnion([Q0]), "depth" : 6 * mm, "offsetDistance" : 25 * mm});
        }
        {
            var Q0;
            Q0=makeQuery(id+"F18.opExtrude","CAP_FACE",FACE,{"disambiguationData":[OSD([sQuery(id+"F17.wireOp",EDGE,"E20"),sQuery(id+"F17.wireOp",EDGE,"E22"),sQuery(id+"F17.wireOp",EDGE,"E24"),sQuery(id+"F17.wireOp",EDGE,"E25")])],"isStart":false});
            var sketch = newSketch(context, id + "F19", { "sketchPlane" : qUnion([Q0])});
            skArc(sketch, "E34.0", {"start": v(-6.75, 54.58) * mm, "mid": v(-23.86, 49.55) * mm, "end": v(-38.47, 39.31) * mm});
            skCircle(sketch, "E35", {"center": v(0, 0) * mm, "radius": 55 * mm});
            skCircle(sketch, "E36.0", {"center": v(0, 0) * mm, "radius": 39 * mm});
            skSolve(sketch);
        }
        {
            var Q0;
            Q0 = qSketchRegion(id + "F19", true);
            extrude(context, id + "F20", {"entities" : qUnion([Q0]), "depth" : 1.5 * mm, "offsetDistance" : 25 * mm});
        }
        {
            var Q0;
            Q0=makeQuery(id+"F20.opExtrude","CAP_EDGE",EDGE,{"disambiguationData":[OSD([sQuery(id+"F19.wireOp",EDGE,"E35")])],"isStart":false});
            fillet(context, id + "F21", {"entities" : qUnion([Q0]), "radius" : 1 * mm, "tangentPropagation" : true, "allowEdgeOverflow" : false});
        }
        {
            var Q0;
            Q0=makeQuery(id+"F20.opExtrude","CAP_FACE",FACE,{"disambiguationData":[OSD([sQuery(id+"F19.wireOp",EDGE,"E35"),sQuery(id+"F19.wireOp",EDGE,"E36.0")])],"isStart":true});
            var sketch = newSketch(context, id + "F22", { "sketchPlane" : qUnion([Q0])});
            skCircle(sketch, "E37.0", {"center": v(0, 0) * mm, "radius": 50 * mm});
            skCircle(sketch, "E38.0", {"center": v(0, 0) * mm, "radius": 55 * mm});
            skCircle(sketch, "E39.0", {"center": v(0, 0) * mm, "radius": 42 * mm});
            skCircle(sketch, "E40.0", {"center": v(0, 0) * mm, "radius": 39 * mm});
            skSolve(sketch);
        }
        {
            var Q0;
            Q0=makeQuery(id+"F22.imprint","IMPRINT",FACE,{"disambiguationData":[TD([[makeQuery(id+"F22.imprint","IMPRINT",EDGE,{"derivedFrom":sQuery(id+"F22.wireOp",EDGE,"E37.0")}),1.0]])]});
            var Q1;
            Q1=makeQuery(id+"F22.imprint","IMPRINT",FACE,{"disambiguationData":[TD([[makeQuery(id+"F22.imprint","IMPRINT",EDGE,{"derivedFrom":sQuery(id+"F22.wireOp",EDGE,"E39.0")}),-1.0]])]});
            extrude(context, id + "F23", {"entities" : qUnion([Q0, Q1]), "operationType" : NewBodyOperationType.ADD, "depth" : 2 * mm, "offsetDistance" : 25 * mm});
        }
    });
